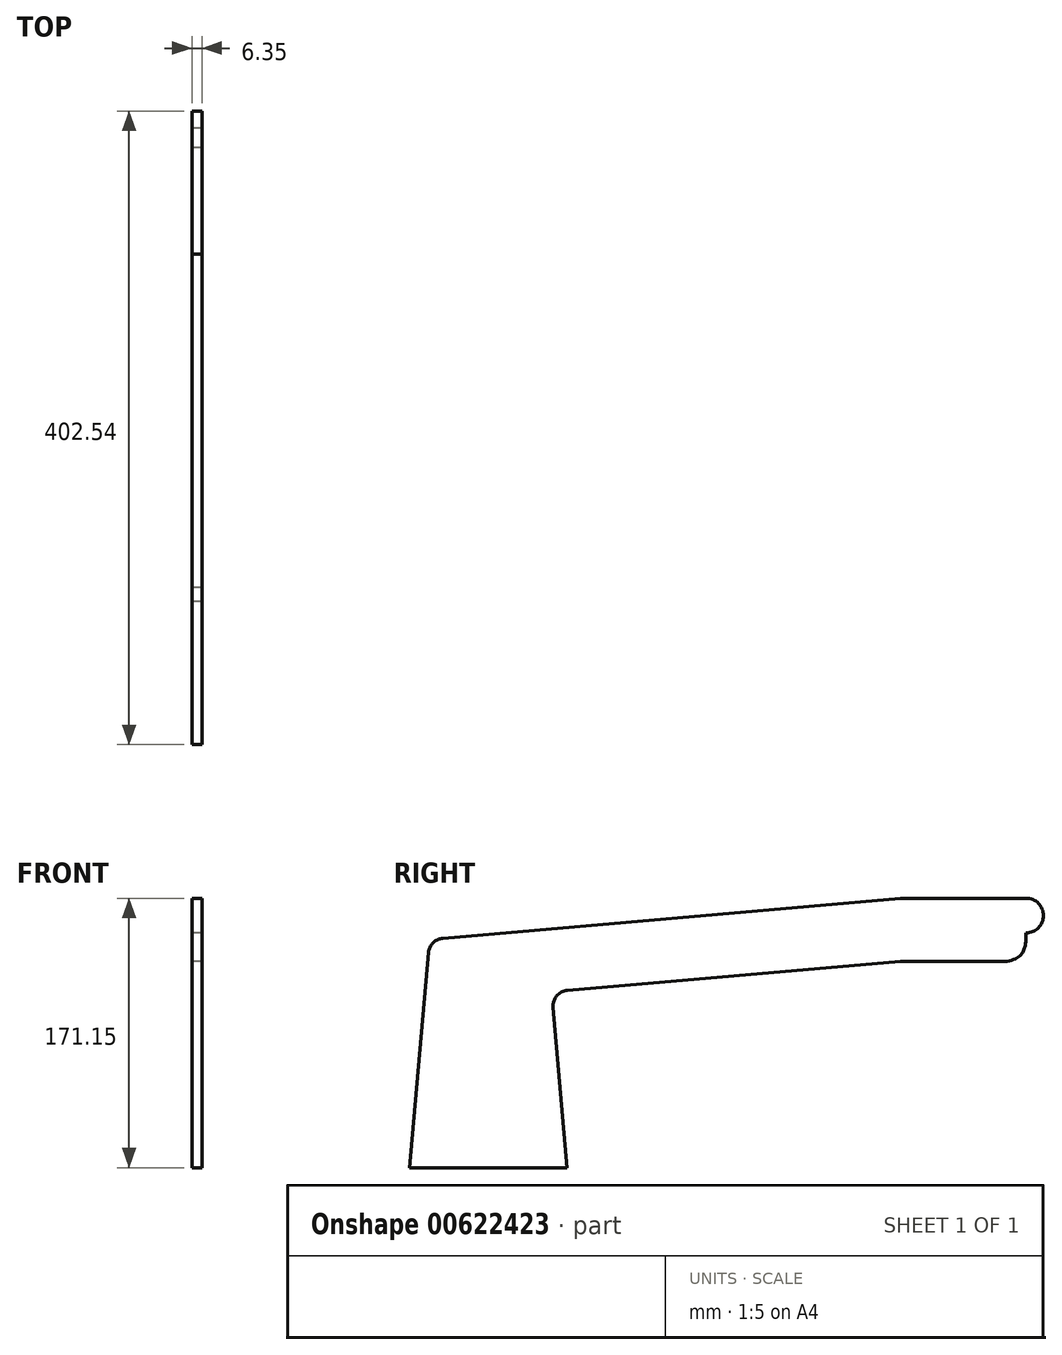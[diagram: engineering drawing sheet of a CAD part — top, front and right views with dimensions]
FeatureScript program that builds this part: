
annotation { "Feature Type Name" : "Feature", "Feature Type Description" : "" }
export const myFeature = defineFeature(function(context is Context, id is Id, definition is map)
    precondition{}
    {
        {
            var Q0;
            Q0=qCreatedBy(makeId("Right.planeOp"),FACE);
            var sketch = newSketch(context, id + "F0", { "sketchPlane" : qUnion([Q0])});
            skLineSegment(sketch, "E0", {"start": v(-38.05, -8.36) * mm, "end": v(-50, -145) * mm});
            skLineSegment(sketch, "E1", {"start": v(50, -145) * mm, "end": v(41.1, -43.18) * mm});
            skLineSegment(sketch, "E2", {"start": v(-50, -145) * mm, "end": v(50, -145) * mm});
            skLineSegment(sketch, "E3", {"start": v(-28.96, 0.73) * mm, "end": v(261.54, 26.15) * mm});
            skLineSegment(sketch, "E4", {"start": v(50.18, -32.35) * mm, "end": v(261.54, -13.85) * mm});
            skLineSegment(sketch, "E5", {"start": v(261.54, 26.15) * mm, "end": v(341.54, 26.15) * mm});
            skLineSegment(sketch, "E6", {"start": v(261.54, -13.85) * mm, "end": v(329.38, -13.85) * mm});
            skLineSegment(sketch, "E7", {"start": v(341.54, 4.15) * mm, "end": v(341.54, 28.15) * mm});
            skArc(sketch, "E8", {"start": v(341.54, 4.15) * mm, "mid": v(352.54, 15.15) * mm, "end": v(341.54, 26.15) * mm});
            skFitSpline(sketch, "E9", {"points": [v(341.54, 4.15) * mm, v(329.38, -13.85) * mm], "startDerivative": vector(0, -21.89) * mm, "endDerivative": vector(-36.5, -5.42) * mm});
            skPoint(sketch, "E10.center.orphan", {"position": v(341.54, 6.15) * mm});
            skPoint(sketch, "E11.orphan", {"position": v(341.54, -13.85) * mm});
            skPoint(sketch, "E12.visualSharp", {"position": v(40.22, -33.22) * mm});
            skArc(sketch, "E12.filletArc", {"start": v(50.18, -32.35) * mm, "mid": v(43.4, -35.88) * mm, "end": v(41.1, -43.18) * mm});
            skPoint(sketch, "E13.visualSharp", {"position": v(-37.31, 0) * mm});
            skArc(sketch, "E13.filletArc", {"start": v(-28.96, 0.73) * mm, "mid": v(-35.15, -2.16) * mm, "end": v(-38.05, -8.36) * mm});
            skSolve(sketch);
        }
        {
            var Q0;
            Q0 = qSketchRegion(id + "F0", true);
            extrude(context, id + "F1", {"entities" : qUnion([Q0]), "depth" : 6.35 * mm, "offsetDistance" : 25 * mm});
        }
    });
